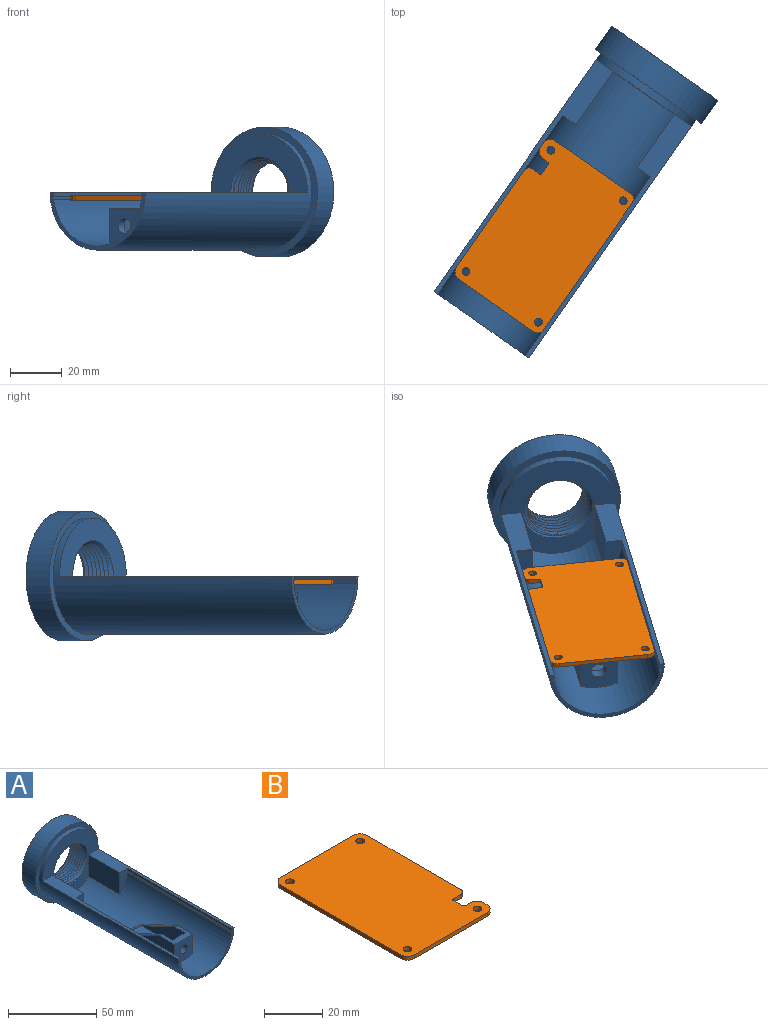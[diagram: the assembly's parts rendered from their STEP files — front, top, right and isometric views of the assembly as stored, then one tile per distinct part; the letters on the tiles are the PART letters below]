
ASSEMBLY  parts=2 mates=1
PART A: 37 faces, bbox 50x123.6x50 mm
  f0: plane 31.14x14.52mm, normal (0,0.42,0.91), area 170.1mm2, adj f2,f29,f30,f31,f34,f35,f36
  f1: cylinder r=3mm len=6mm, axis (0,-1,0), area 75.4mm2, adj f32,f33
  f2: cylinder r=20.85mm len=108.9mm, axis (0,1,0), area 5163.6mm2, adj f0,f3,f6,f14,f16,f17,f26,f27
  f3: plane 83.9x0.57mm, normal (0,0,1), area 47.6mm2, adj f2,f19,f27,f28
  f4: cylinder r=22.35mm len=111.9mm, axis (0,1,0), area 8067.7mm2, adj f5,f6,f15,f21,f28
  f5: plane 108.9x8mm, normal (0,0,1), area 346.8mm2, adj f4,f6,f14,f23,f26,f28
  f6: plane 44.7x43.2mm, normal (0,-1,0), area 746.3mm2, adj f2,f4,f5,f10,f14,f15,f16
  f7: cylinder r=11.65mm len=23.3mm, axis (0,-1,0), area 1.6mm2, adj f9,f11,f12,f13
  f8: plane 50x50mm, normal (0,1,0), area 1378.1mm2, adj f9,f20
  f9: cone r=11.65mm half-angle=45deg, axis (0,1,0), area 144.3mm2, adj f7,f8,f12,f13
  f10: cone r=11.65mm half-angle=45deg, axis (0,-1,0), area 131.3mm2, adj f6,f11,f12,f13
  f11: cone r=11.65mm half-angle=45deg, axis (0,-1,0), area 13mm2, adj f7,f10,f12,f13
  f12: bspline ~30.37x26.3mm, area 870.5mm2, adj f7,f9,f10,f11,f13
  f13: bspline ~30.37x26.3mm, area 867.1mm2, adj f7,f9,f10,f11,f12
  f14: plane 25x15.13mm, normal (1,0,0), area 378.2mm2, adj f2,f5,f6,f26
  f15: plane 108.9x8mm, normal (0,0,1), area 346.8mm2, adj f4,f6,f16,f24,f27,f28
  f16: plane 25x15.13mm, normal (-1,0,0), area 378.2mm2, adj f2,f6,f15,f27
  f17: plane 83.9x0.57mm, normal (0,0,1), area 47.6mm2, adj f2,f18,f26,f28
  f18: plane 83.9x1.4mm, normal (1,0,0), area 117.5mm2, adj f17,f22,f26,f28
  f19: plane 83.9x1.4mm, normal (-1,0,0), area 117.5mm2, adj f3,f25,f27,f28
  f20: cylinder r=25mm len=50mm, axis (0,1,0), area 1727.9mm2, adj f8,f21
  f21: plane 50x50mm, normal (0,-1,0), area 394.2mm2, adj f4,f20
  f22: plane 83.9x0.6mm, normal (0,0,-1), area 50.3mm2, adj f18,f23,f26,f28
  f23: plane 83.9x1.6mm, normal (1,0,0), area 134.2mm2, adj f5,f22,f26,f28
  f24: plane 83.9x1.6mm, normal (-1,0,0), area 134.2mm2, adj f15,f25,f27,f28
  f25: plane 83.9x0.6mm, normal (0,0,-1), area 50.3mm2, adj f19,f24,f27,f28
  f26: plane 15.13x6.85mm, normal (0,-1,0), area 68.2mm2, adj f2,f5,f14,f17,f18,f22,f23
  f27: plane 15.13x6.85mm, normal (0,-1,0), area 68.2mm2, adj f2,f3,f15,f16,f19,f24,f25
  f28: plane 44.7x22.35mm, normal (0,-1,0), area 101.2mm2, adj f2,f3,f4,f5,f15,f17,f18,f19
  f29: plane 40.68x13.26mm, normal (-1,0,0), area 350.9mm2, adj f0,f2,f31,f32
  f30: plane 40.68x13.26mm, normal (1,0,0), area 350.9mm2, adj f0,f2,f31,f32
  f31: plane 14.26x12.23mm, normal (0,0,1), area 90mm2, adj f0,f29,f30,f32,f33,f34,f35
  f32: plane 14.52x14.26mm, normal (0,-1,0), area 172.9mm2, adj f1,f2,f29,f30,f31
  f33: plane 12.6x10.26mm, normal (0,1,0), area 101mm2, adj f1,f31,f34,f35,f36
  f34: plane 35.25x12.6mm, normal (1,0,0), area 274mm2, adj f0,f31,f33,f36
  f35: plane 35.25x12.6mm, normal (-1,0,0), area 274mm2, adj f0,f31,f33,f36
  f36: plane 35.25x10.26mm, normal (0,0,1), area 361.8mm2, adj f0,f33,f34,f35
PART B: 23 faces, bbox 42x65x1.6 mm
  f0: plane 11.8x1.6mm, normal (1,0,0), area 18.9mm2, adj f1,f20,f21,f22
  f1: plane 33.31x1.6mm, normal (1,0,0), area 53.3mm2, adj f0,f2,f21,f22
  f2: cylinder r=3.74mm len=3.75mm, axis (0,0,-1), area 9.4mm2, adj f1,f3,f21,f22
  f3: plane 34.63x1.6mm, normal (0,1,0), area 55.4mm2, adj f2,f4,f21,f22
  f4: cylinder r=3.62mm len=3.62mm, axis (0,0,-1), area 9.1mm2, adj f3,f5,f21,f22
  f5: plane 58.21x1.6mm, normal (-1,0,0), area 93.1mm2, adj f4,f6,f21,f22
  f6: cylinder r=3.17mm len=3.18mm, axis (0,0,-1), area 8mm2, adj f5,f7,f21,f22
  f7: plane 35.56x1.6mm, normal (0,-1,0), area 56.9mm2, adj f6,f8,f21,f22
  f8: cylinder r=3.17mm len=3.18mm, axis (0,0,-1), area 8mm2, adj f7,f9,f21,f22
  f9: plane 1.91x1.6mm, normal (1,0,0), area 3mm2, adj f8,f10,f21,f22
  f10: cylinder r=3.17mm len=3.18mm, axis (0,0,-1), area 8mm2, adj f9,f11,f21,f22
  f11: plane 2.54x1.6mm, normal (0,1,0), area 4.1mm2, adj f10,f12,f21,f22
  f12: cylinder r=0.64mm len=1.6mm, axis (0,0,-1), area 1.6mm2, adj f11,f13,f21,f22
  f13: plane 4.45x1.6mm, normal (1,0,0), area 7.1mm2, adj f12,f14,f21,f22
  f14: cylinder r=0.64mm len=1.6mm, axis (0,0,-1), area 1.6mm2, adj f13,f15,f21,f22
  f15: plane 3.55x1.6mm, normal (0,-1,0), area 5.7mm2, adj f14,f20,f21,f22
  f16: cylinder r=1.5mm len=3mm, axis (0,0,-1), area 15.1mm2, adj f21,f22
  f17: cylinder r=1.5mm len=3mm, axis (0,0,-1), area 15.1mm2, adj f21,f22
  f18: cylinder r=1.5mm len=3mm, axis (0,0,-1), area 15.1mm2, adj f21,f22
  f19: cylinder r=1.5mm len=3mm, axis (0,0,-1), area 15.1mm2, adj f21,f22
  f20: cylinder r=2.17mm len=2.17mm, axis (0,0,-1), area 5.4mm2, adj f0,f15,f21,f22
  f21: plane 65x41.99mm, normal (0,0,1), area 2648.1mm2, adj f0,f1,f2,f3,f4,f5,f6,f7
  f22: plane 65x41.99mm, normal (0,0,-1), area 2648.1mm2, adj f0,f1,f2,f3,f4,f5,f6,f7
PLACE A rot(axis=(0,0,-1),35deg) t=(-21.68,3.36,3.22)mm
PLACE B rot(axis=(0,0,1),145deg) t=(-68.07,-63.25,0.12)mm
MATE fastened A.f19 <-> B.f5  axis (-0.82,0.57,0) through (-50.75,-75.11,0.92)mm
